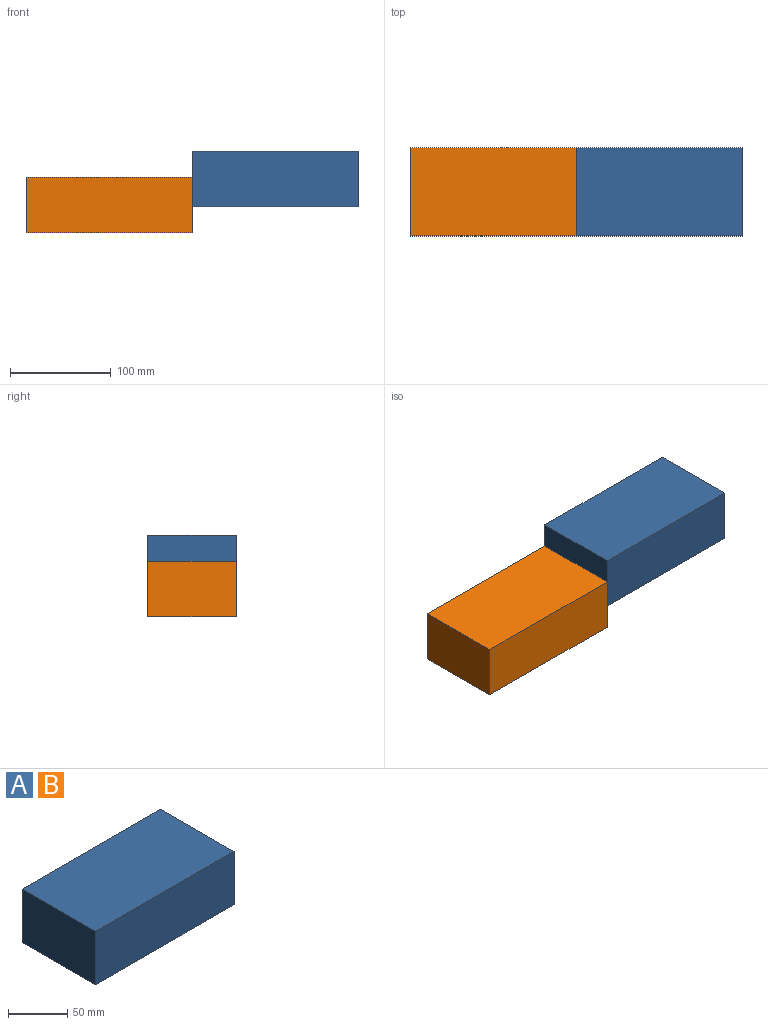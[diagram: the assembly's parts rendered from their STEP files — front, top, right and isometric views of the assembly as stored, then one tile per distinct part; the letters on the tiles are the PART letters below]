
ASSEMBLY  parts=2 mates=1
PART A: 11 faces, bbox 165x87.5x55 mm
  f0: plane 87.5x55mm, normal (1,0,0), area 4812.5mm2, adj f1,f3,f4,f5
  f1: plane 165x55mm, normal (0,-1,0), area 9075mm2, adj f0,f2,f4,f5
  f2: plane 87.5x55mm, normal (-1,0,0), area 4812.5mm2, adj f1,f3,f4,f5
  f3: plane 165x55mm, normal (0,1,0), area 9075mm2, adj f0,f2,f4,f5
  f4: plane 165x87.5mm, normal (0,0,-1), area 2425mm2, adj f0,f1,f2,f3,f6,f7,f8,f9
  f5: plane 165x87.5mm, normal (0,0,1), area 14437.5mm2, adj f0,f1,f2,f3
  f6: plane 77.5x50mm, normal (-1,0,0), area 3875mm2, adj f4,f7,f9,f10
  f7: plane 155x50mm, normal (0,1,0), area 7750mm2, adj f4,f6,f8,f10
  f8: plane 77.5x50mm, normal (1,0,0), area 3875mm2, adj f4,f7,f9,f10
  f9: plane 155x50mm, normal (0,-1,0), area 7750mm2, adj f4,f6,f8,f10
  f10: plane 155x77.5mm, normal (0,0,-1), area 12012.5mm2, adj f6,f7,f8,f9
PART B: same geometry as A
PLACE A at identity fixed
PLACE B t=(-165,0,-25.7)mm
MATE planar A.f2 <-> B.f0  axis (-1,0,0) through (-82.5,0,-29.5)mm
